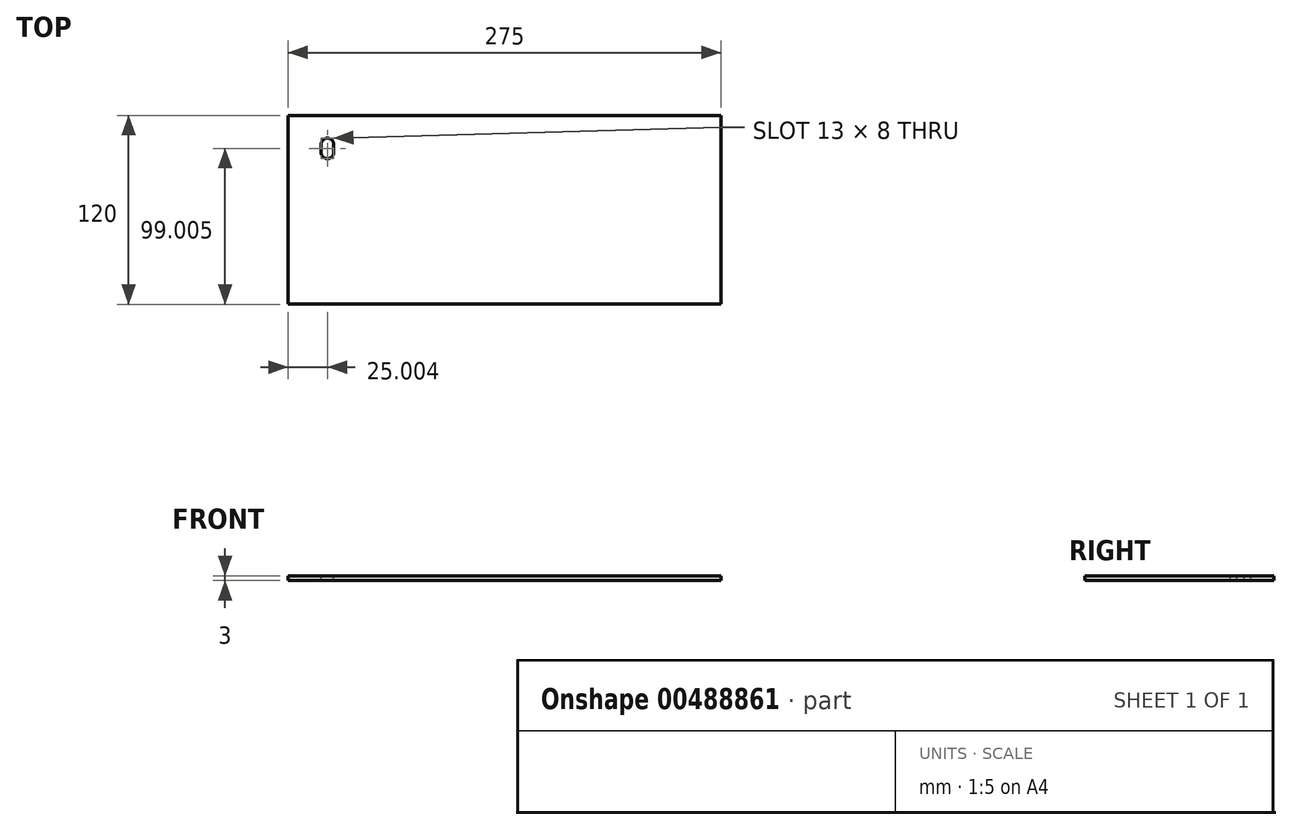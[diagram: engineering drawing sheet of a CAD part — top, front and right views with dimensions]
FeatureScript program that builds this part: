
annotation { "Feature Type Name" : "Feature", "Feature Type Description" : "" }
export const myFeature = defineFeature(function(context is Context, id is Id, definition is map)
    precondition{}
    {
        {
            var Q0;
            Q0=qCreatedBy(makeId("Top.planeOp"),FACE);
            var sketch = newSketch(context, id + "F0", { "sketchPlane" : qUnion([Q0])});
            skLineSegment(sketch, "E0.bottom", {"start": v(-131.3, 61.62) * mm, "end": v(143.7, 61.62) * mm});
            skLineSegment(sketch, "E0.top", {"start": v(-131.3, -58.38) * mm, "end": v(143.7, -58.38) * mm});
            skLineSegment(sketch, "E0.left", {"start": v(-131.3, 61.62) * mm, "end": v(-131.3, -58.38) * mm});
            skLineSegment(sketch, "E0.right", {"start": v(143.7, 61.62) * mm, "end": v(143.7, -58.38) * mm});
            skSolve(sketch);
        }
        {
            var Q0;
            Q0=makeQuery(id+"F0.imprint","IMPRINT",FACE,{"disambiguationData":[TD([[makeQuery(id+"F0.imprint","IMPRINT",EDGE,{"derivedFrom":sQuery(id+"F0.wireOp",EDGE,"E0.bottom")}),-1.0]])]});
            extrude(context, id + "F1", {"entities" : qUnion([Q0]), "depth" : 3 * mm});
        }
        {
            var Q0;
            Q0=makeQuery(id+"F1.opExtrude","CAP_FACE",FACE,{"disambiguationData":[OSD([sQuery(id+"F0.wireOp",EDGE,"E0.bottom"),sQuery(id+"F0.wireOp",EDGE,"E0.top"),sQuery(id+"F0.wireOp",EDGE,"E0.left"),sQuery(id+"F0.wireOp",EDGE,"E0.right")])],"isStart":false});
            var sketch = newSketch(context, id + "F2", { "sketchPlane" : qUnion([Q0])});
            skArc(sketch, "E1", {"start": v(-102.3, 43.04) * mm, "mid": v(-106.3, 47.12) * mm, "end": v(-110.3, 43.04) * mm});
            skArc(sketch, "E2", {"start": v(-110.3, 38.21) * mm, "mid": v(-106.35, 34.12) * mm, "end": v(-102.3, 38.13) * mm});
            skLineSegment(sketch, "E3", {"start": v(-110.3, 43.21) * mm, "end": v(-110.3, 38.04) * mm});
            skLineSegment(sketch, "E4", {"start": v(-102.3, 43.21) * mm, "end": v(-102.3, 38.13) * mm});
            skSolve(sketch);
        }
        {
            var Q0;
            Q0 = qSketchRegion(id + "F2", true);
            extrude(context, id + "F3", {"entities" : qUnion([Q0]), "operationType" : NewBodyOperationType.REMOVE, "oppositeDirection" : true, "depth" : 3 * mm, "offsetDistance" : 25 * mm});
        }
    });
